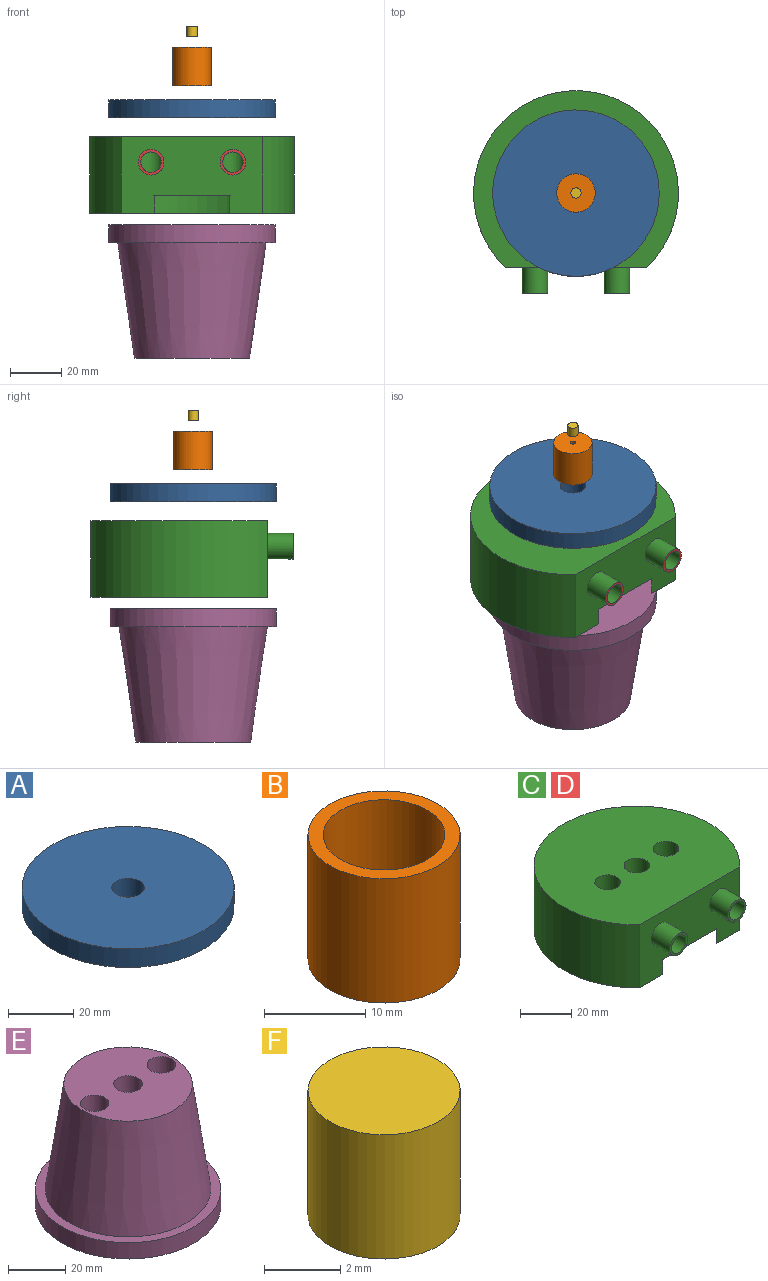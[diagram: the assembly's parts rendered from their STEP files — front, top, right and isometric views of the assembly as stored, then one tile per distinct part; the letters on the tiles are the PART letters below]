
ASSEMBLY  parts=6 mates=4
PART A: 4 faces, bbox 65x65x7 mm
  f0: cylinder r=32.5mm len=65mm, axis (0,0,-1), area 1429.4mm2, adj f1,f2
  f1: plane 65x65mm, normal (0,0,1), area 3239.8mm2, adj f0,f3
  f2: plane 65x65mm, normal (0,0,-1), area 3239.8mm2, adj f0,f3
  f3: cylinder r=5mm len=10mm, axis (0,0,-1), area 219.9mm2, adj f1,f2
PART B: 6 faces, bbox 15x15x15 mm
  f0: cylinder r=7.5mm len=15mm, axis (0,0,-1), area 706.9mm2, adj f1,f2
  f1: plane 15x15mm, normal (0,0,1), area 63.6mm2, adj f0,f3
  f2: plane 15x15mm, normal (0,0,-1), area 173.6mm2, adj f0,f5
  f3: cylinder r=6mm len=12mm, axis (0,0,1), area 452.4mm2, adj f1,f4
  f4: plane 12x12mm, normal (0,0,1), area 110mm2, adj f3,f5
  f5: cylinder r=1mm len=3mm, axis (0,0,-1), area 18.8mm2, adj f2,f4
PART C: 15 faces, bbox 80x79x30 mm
  f0: plane 80x69mm, normal (0,0,1), area 4374.3mm2, adj f1,f3,f4,f5,f8
  f1: cylinder r=40mm len=80mm, axis (0,0,-1), area 5716.4mm2, adj f0,f2,f8
  f2: plane 80x69mm, normal (0,0,-1), area 1360.8mm2, adj f1,f6,f8
  f3: cylinder r=5mm len=23mm, axis (0,0,-1), area 722.6mm2, adj f0,f7
  f4: cylinder r=5mm len=23mm, axis (0,0,-1), area 666.8mm2, adj f0,f7,f9
  f5: cylinder r=5mm len=23mm, axis (0,0,-1), area 666.8mm2, adj f0,f7,f10
  f6: cylinder r=32.5mm len=65mm, axis (0,0,-1), area 1216.3mm2, adj f2,f7,f8
  f7: plane 65x61.5mm, normal (0,0,-1), area 3013.4mm2, adj f3,f4,f5,f6,f8
  f8: plane 55.1x30mm, normal (0,-1,0), area 1290.5mm2, adj f0,f1,f2,f6,f7,f11,f13
  f9: cylinder r=4mm len=36mm, axis (0,-1,0), area 878.1mm2, adj f4,f14
  f10: cylinder r=4mm len=36mm, axis (0,-1,0), area 878.1mm2, adj f5,f12
  f11: cylinder r=5mm len=10mm, axis (0,1,0), area 314.2mm2, adj f8,f12
  f12: plane 10x10mm, normal (0,-1,0), area 28.3mm2, adj f10,f11
  f13: cylinder r=5mm len=10mm, axis (0,1,0), area 314.2mm2, adj f8,f14
  f14: plane 10x10mm, normal (0,-1,0), area 28.3mm2, adj f9,f13
PART D: same geometry as C
PART E: 8 faces, bbox 65x65x52 mm
  f0: cylinder r=32.5mm len=65mm, axis (0,0,-1), area 1429.4mm2, adj f1,f2
  f1: plane 65x65mm, normal (0,0,1), area 676.2mm2, adj f0,f4
  f2: plane 65x65mm, normal (0,0,-1), area 3082.7mm2, adj f0,f5,f6,f7
  f3: plane 45x45mm, normal (0,0,1), area 1354.8mm2, adj f4,f5,f6,f7
  f4: cone r=29mm half-angle=8.2deg, axis (0,0,-1), area 7356.2mm2, adj f1,f3
  f5: cylinder r=5mm len=52mm, axis (0,0,-1), area 1633.6mm2, adj f2,f3
  f6: cylinder r=5mm len=52mm, axis (0,0,-1), area 1633.6mm2, adj f2,f3
  f7: cylinder r=5mm len=52mm, axis (0,0,-1), area 1633.6mm2, adj f2,f3
PART F: 3 faces, bbox 4x4x4 mm
  f0: cylinder r=2mm len=4mm, axis (0,0,-1), area 50.3mm2, adj f1,f2
  f1: plane 4x4mm, normal (0,0,1), area 12.6mm2, adj f0
  f2: plane 4x4mm, normal (0,0,-1), area 12.6mm2, adj f0
PLACE A t=(0.11,-1.3,21.05)mm
PLACE B rot(axis=(0,1,0),180deg) t=(0.11,-1.3,48.64)mm
PLACE C t=(0.11,-1.3,-16.29)mm
PLACE D t=(0.11,-1.3,-16.29)mm fixed
PLACE E rot(axis=(0,1,0),180deg) t=(0.11,-1.3,-20.76)mm
PLACE F t=(0.11,-1.3,52.91)mm
MATE slider B.f3 <-> A.f0  axis (0,0,-1) through (0.11,-1.3,33.64)mm
MATE slider F.f0 <-> B.f5  axis (0,0,1) through (0.11,-1.3,56.91)mm
MATE slider A.f0 <-> D.f1  axis (0,0,1) through (0.11,-1.3,28.05)mm
MATE slider E.f0 <-> D.f3  axis (0,0,1) through (0.11,-1.3,-20.76)mm
